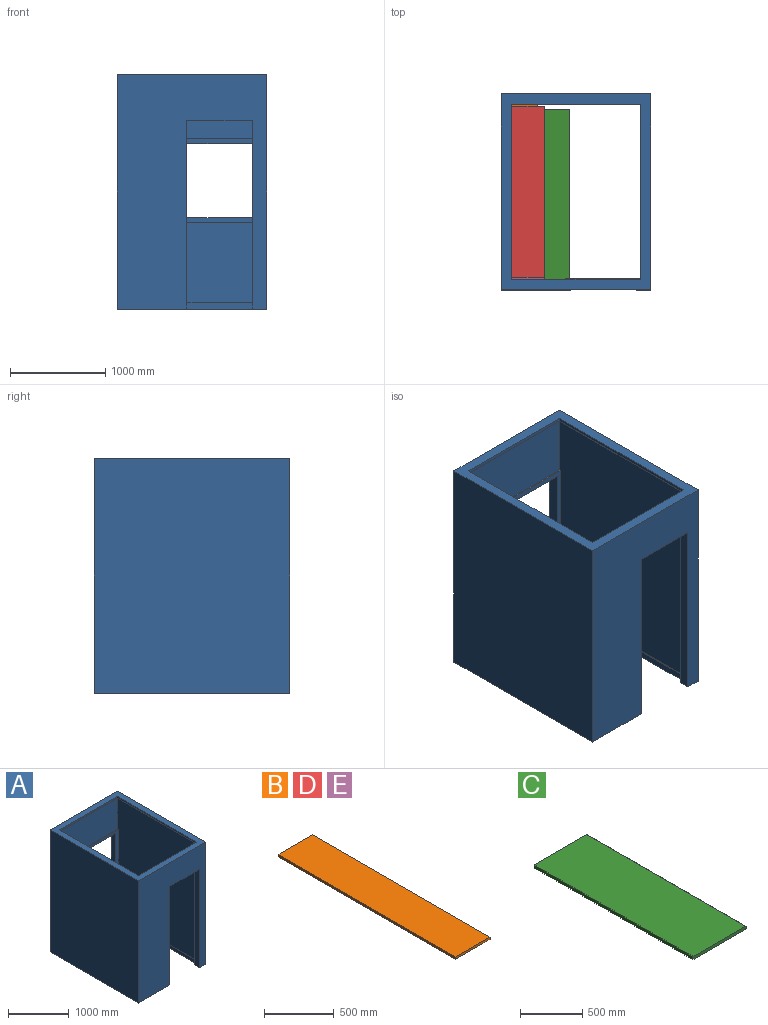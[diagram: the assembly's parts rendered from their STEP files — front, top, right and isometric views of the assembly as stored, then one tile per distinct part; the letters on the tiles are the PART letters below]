
ASSEMBLY  parts=5 mates=9
PART A: 34 faces, bbox 1570x2060x2461 mm
  f0: plane 2036x793mm, normal (0,1,0), area 237638mm2, adj f2,f6,f10,f11,f12,f13,f14,f23
  f1: plane 2357x1370mm, normal (0,-1,0), area 2526690mm2, adj f6,f8,f15,f16,f17,f27,f33
  f2: plane 2060x1570mm, normal (0,0,-1), area 668734mm2, adj f0,f3,f4,f5,f9,f10,f12,f14
  f3: plane 2461x2060mm, normal (1,0,0), area 5069660mm2, adj f2,f4,f9,f32
  f4: plane 2461x1570mm, normal (0,1,0), area 3319170mm2, adj f2,f3,f5,f19,f20,f21,f22,f32
  f5: plane 2461x2060mm, normal (-1,0,0), area 5069660mm2, adj f2,f4,f9,f32
  f6: plane 2357x1860mm, normal (-1,0,0), area 4344176mm2, adj f0,f1,f7,f11,f15,f17,f18,f27
  f7: plane 2357x1370mm, normal (0,1,0), area 1668466mm2, adj f6,f8,f10,f11,f27,f33
  f8: plane 2357x1860mm, normal (1,0,0), area 4384020mm2, adj f1,f7,f27,f33
  f9: plane 2461x1570mm, normal (0,-1,0), area 2487472mm2, adj f2,f3,f5,f12,f13,f14,f32
  f10: plane 2036x14mm, normal (-1,0,0), area 27892mm2, adj f0,f2,f7,f11,f26,f27
  f11: plane 793x14mm, normal (0,0,1), area 11102mm2, adj f0,f6,f7,f10
  f12: plane 1986x114mm, normal (-1,0,0), area 226404mm2, adj f0,f2,f9,f13
  f13: plane 693x114mm, normal (0,0,-1), area 79002mm2, adj f0,f9,f12,f14
  f14: plane 1986x114mm, normal (1,0,0), area 226404mm2, adj f0,f2,f9,f13
  f15: plane 800x14mm, normal (0,0,1), area 11200mm2, adj f1,f6,f16,f18
  f16: plane 878x14mm, normal (-1,0,0), area 12292mm2, adj f1,f15,f17,f18
  f17: plane 800x14mm, normal (0,0,-1), area 11200mm2, adj f1,f6,f16,f18
  f18: plane 878x800mm, normal (0,-1,0), area 157800mm2, adj f6,f15,f16,f17,f19,f20,f21,f22
  f19: plane 778x114mm, normal (-1,0,0), area 88692mm2, adj f4,f18,f20,f22
  f20: plane 700x114mm, normal (0,0,1), area 79800mm2, adj f4,f18,f19,f21
  f21: plane 778x114mm, normal (1,0,0), area 88692mm2, adj f4,f18,f20,f22
  f22: plane 700x114mm, normal (0,0,-1), area 79800mm2, adj f4,f18,f19,f21
  f23: plane 1837x68mm, normal (-1,0,0), area 124916mm2, adj f0,f2,f24,f27
  f24: plane 1352x68mm, normal (0,-1,0), area 91936mm2, adj f2,f23,f25,f27
  f25: plane 1842x68mm, normal (1,0,0), area 125256mm2, adj f2,f24,f26,f27
  f26: plane 568x68mm, normal (0,1,0), area 38624mm2, adj f2,f10,f25,f27
  f27: plane 1860x1370mm, normal (0,0,1), area 50634mm2, adj f0,f1,f6,f7,f8,f10,f23,f24
  f28: plane 1354x36mm, normal (0,1,0), area 48744mm2, adj f29,f31,f32,f33
  f29: plane 1844x36mm, normal (1,0,0), area 66384mm2, adj f28,f30,f32,f33
  f30: plane 1354x36mm, normal (0,-1,0), area 48744mm2, adj f29,f31,f32,f33
  f31: plane 1844x36mm, normal (-1,0,0), area 66384mm2, adj f28,f30,f32,f33
  f32: plane 2060x1570mm, normal (0,0,1), area 737424mm2, adj f3,f4,f5,f9,f28,f29,f30,f31
  f33: plane 1860x1370mm, normal (0,0,-1), area 51424mm2, adj f1,f6,f7,f8,f28,f29,f30,f31
PART B: 6 faces, bbox 350x1800x20 mm
  f0: plane 1800x20mm, normal (-1,0,0), area 36000mm2, adj f1,f3,f4,f5
  f1: plane 350x20mm, normal (0,-1,0), area 7000mm2, adj f0,f2,f4,f5
  f2: plane 1800x20mm, normal (1,0,0), area 36000mm2, adj f1,f3,f4,f5
  f3: plane 350x20mm, normal (0,1,0), area 7000mm2, adj f0,f2,f4,f5
  f4: plane 1800x350mm, normal (0,0,1), area 630000mm2, adj f0,f1,f2,f3
  f5: plane 1800x350mm, normal (0,0,-1), area 630000mm2, adj f0,f1,f2,f3
PART C: 8 faces, bbox 600x1800x30 mm
  f0: plane 1800x30mm, normal (-1,0,0), area 54000mm2, adj f1,f3,f4,f5
  f1: plane 600x30mm, normal (0,-1,0), area 17989.3mm2, adj f0,f2,f4,f5,f6,f7
  f2: plane 1800x20mm, normal (1,0,0), area 36000mm2, adj f1,f3,f6,f7
  f3: plane 600x30mm, normal (0,1,0), area 17989.3mm2, adj f0,f2,f4,f5,f6,f7
  f4: plane 1800x595mm, normal (0,0,1), area 1071000mm2, adj f0,f1,f3,f7
  f5: plane 1800x595mm, normal (0,0,-1), area 1071000mm2, adj f0,f1,f3,f6
  f6: cylinder r=5mm len=1800mm, axis (0,1,0), area 14137.2mm2, adj f1,f2,f3,f5
  f7: cylinder r=5mm len=1800mm, axis (0,-1,0), area 14137.2mm2, adj f1,f2,f3,f4
PART D: same geometry as B
PART E: same geometry as B
PLACE A t=(0,100,0)mm fixed
PLACE B rot(axis=(0,0,1),180deg) t=(-1094.67,1950.47,1565.92)mm
PLACE C t=(-1350,100,650)mm
PLACE D rot(axis=(0,0,-1),180deg) t=(-1020,1930,2036.5)mm
PLACE E t=(-1370,100,1218.43)mm
MATE parallel A.f8 <-> E.f0  axis (1,0,0) through (-1370,1030,1246.5)mm
MATE parallel E.f4 <-> B.f4  axis (0,0,1) through (-1195,1000,1238.43)mm
MATE parallel B.f2 <-> A.f8  axis (-1,0,0) through (-1444.67,1050.47,1575.92)mm
MATE parallel A.f8 <-> C.f0  axis (1,0,0) through (-1370,1030,1246.5)mm
MATE parallel E.f1 <-> A.f7  axis (0,-1,0) through (-1195,100,1228.43)mm
MATE fastened A.f8 <-> D.f2  axis (1,0,0) through (-1370,1030,1246.5)mm
MATE parallel C.f1 <-> A.f7  axis (0,-1,0) through (-1050.18,100,665)mm
MATE parallel B.f3 <-> A.f7  axis (0,-1,0) through (-1269.67,150.47,1575.92)mm
MATE parallel A.f2 <-> C.f5  axis (0,0,-1) through (-717.42,1139.56,0)mm
